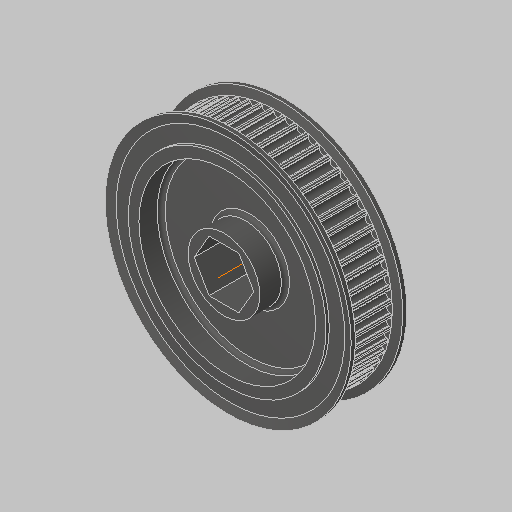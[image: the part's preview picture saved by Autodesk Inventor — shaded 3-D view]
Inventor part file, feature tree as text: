
AUTODESK INVENTOR PART (.ipt)
format: ipt  version: 2023.5 (Build 275446000, 446)  size: 699,904 bytes
history: native  units: in
note: dims shown in document units (in); Inventor stores cm internally (conversion verified against a paired STEP export)
features: plane x1, fillet x1
ambient origin geometry x8: Origin, YZ Plane, XZ Plane, XY Plane, X Axis, Y Axis, Z Axis, Center Point
bodies: Solid1 (feature_tree)
feature tree (2):
  plane  "Work Plane1"
  fillet  "Fillet1"  [1 undecoded]
note: 1 required parameter value undecoded (feature->parameter linkage not recoverable at this tier; creation-order binding heuristic only, values carry confidence <= 0.55)
